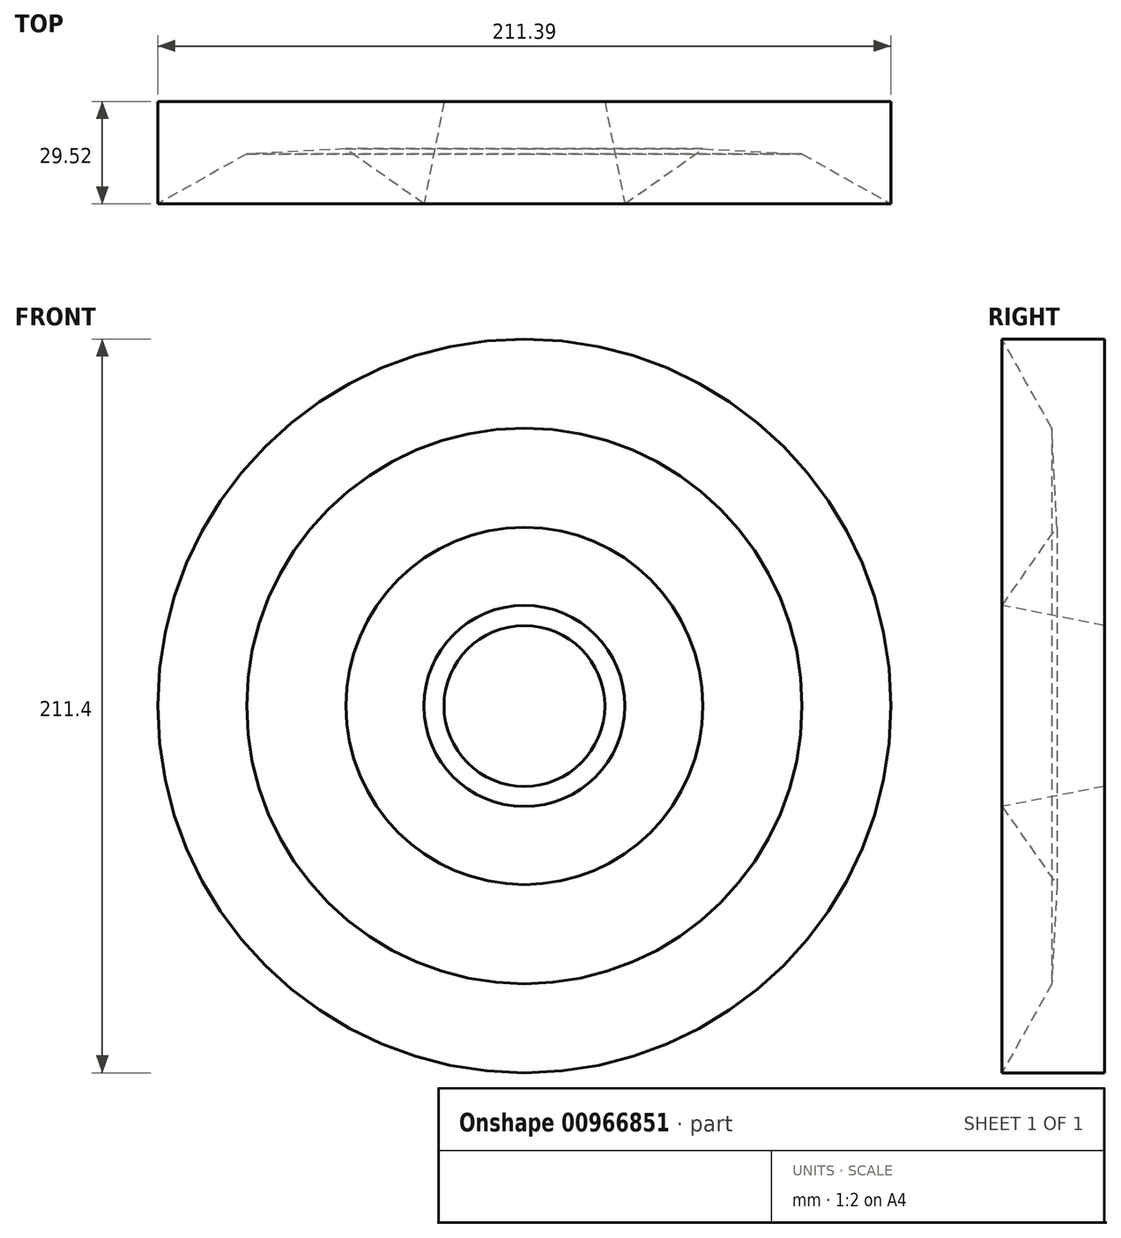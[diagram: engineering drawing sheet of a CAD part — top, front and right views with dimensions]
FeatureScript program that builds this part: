
annotation { "Feature Type Name" : "Feature", "Feature Type Description" : "" }
export const myFeature = defineFeature(function(context is Context, id is Id, definition is map)
    precondition{}
    {
        {
            var Q0;
            Q0=qCreatedBy(makeId("Top.planeOp"),FACE);
            var sketch = newSketch(context, id + "F0", { "sketchPlane" : qUnion([Q0])});
            skLineSegment(sketch, "E0", {"start": v(-39.87, 29.52) * mm, "end": v(42.65, 29.52) * mm});
            skLineSegment(sketch, "E1", {"start": v(42.65, 29.52) * mm, "end": v(42.65, 0) * mm});
            skLineSegment(sketch, "E2", {"start": v(42.65, 0) * mm, "end": v(17.02, 14.35) * mm});
            skLineSegment(sketch, "E3", {"start": v(17.02, 14.35) * mm, "end": v(-11.58, 15.81) * mm});
            skLineSegment(sketch, "E4", {"start": v(-11.58, 15.81) * mm, "end": v(-34.08, 0) * mm});
            skLineSegment(sketch, "E5", {"start": v(-34.08, 0) * mm, "end": v(-39.87, 29.52) * mm});
            skLineSegment(sketch, "E6", {"start": v(-63.05, 64.65) * mm, "end": v(-63.05, -44.6) * mm});
            skSolve(sketch);
        }
        {
            var Q0;
            Q0=makeQuery(id+"F0.imprint","IMPRINT",FACE,{"disambiguationData":[TD([[makeQuery(id+"F0.imprint","IMPRINT",EDGE,{"derivedFrom":sQuery(id+"F0.wireOp",EDGE,"E0")}),-1.0]])]});
            var Q1;
            Q1=sQuery(id+"F0.wireOp",EDGE,"E6");
            revolve(context, id + "F1", {"surfaceOperationType" : NewSurfaceOperationType.NEW, "entities" : qUnion([Q0]), "axis" : qUnion([Q1]), "revolveType" : RevolveType.FULL});
        }
    });
